# Revit family: Pump_Commercial-Sewage_Dewatering-Zoeller-64HD_Single_Seal_6-Series
name_source: partatom
category: Mechanical Equipment
revit_build: Autodesk Revit 2014 (Build: 20130308_1515(x64)
units: mm (PartAtom-declared; Revit-internal decimal feet)

## types (7) — shared parameters
Assembly Code = D2090
Connection Description = 6" Horizontal Discharge
Default Elevation = 0"
Description = Heavy Duty Solids-Handling Pumps
Discharge Diameter = 6"
Discharge Radius = 3"
Flange = ANSI B16.1
Height = 47 1/8"
Hertz = 60
High Temperature (5-10 BHP) = No
Impeller Type = 2 Vane Enclosed
Installation Type = Floor Mounted
Insulation = Class F
Inverted Duty = No
Length = 27 1/8"
Manufacturer = Zoeller
Material = Cast Iron-Zoeller-Powder Coated Epoxy
Max. Stator Temp. = 311 °F
Max. Water Temp. = 104 °F
Min. Recommended Fluid Level = 24"
Moisture Sensor (Optional) = Moisture Sensing Probes (Requires a circuit in control panel)
Motor Design Letter = NEMA B
Motor Shaft = 416 SS
Motor Thermal Shutoff (Single Phase Only) = Thermal Sensors With Automatic Reset
Motor Type = Standard Submersible
O-Rings (Optional) Viton = No
O-Rings and Cover Gasket = Buna-N
Operation = Non-Automatic
Phase = 3
Power Cord = 25' (7.6 m) #2-4 SO
Price = Prices may vary. Please consult Manufacturer Representative for most up-to-date price list.
Product Documentation Link = http://cdn.qleapahead.com
Product Page URL = http://www.zoellerengprod.com
Pump Net Weight: lbs. (kg) = 850 lbs. (386 kg)
RPM = 1725
Rail System Discharge = 6"
Sensor Cord Size = #16-5 SO
Shaft Seal (Standard) = Carbon/Ceramic
Shaft Seal Lower (Options) = Carbon/Silicon Carbide, Silicon Carbide/Silicon Carbide
Shaft Seal Upper (Options) = Silicon Carbide/Carbon, Silicon Carbide/Silicon Carbide
Solid Size = 4" (100 mm)
Tandem Seals = Standard
Trimmed Impeller = No
URL = http://www.zoellerpumps.com
Warranty Information = 36 Months (Limited)
Waste Connection = Yes
Width = 22 1/8"

## per-type parameters (varying)
| type | Amps | Apparent Load | Impeller Diameter | Locked Rotor Amps (Voltage Dependant) | Max. Flow @ 20' | Max. Flow @ 35' | Max. Flow @ 40' | Max. Head | Maximum KW Input | Model | Motor | NEC Locked Rotor Code | Service Factor | Voltage |
| F6424 - 230V/3Ph/68A/25BHP | 68 A | 15640 VA | 9 1/8" | 314 | 1900 GPM | 0 GPM | 0 GPM | 70' | 24.2 | F6424 | 25 | F | 1.2 | 230 V |
| G6424 - 460V/3Ph/34A/25BHP | 34 A | 15640 VA | 9 1/8" | 157 | 1900 GPM | 0 GPM | 0 GPM | 70' | 24.2 | G6424 | 25 | F | 1.2 | 460 V |
| F6425 - 230V/3Ph/80A/30BHP | 80 A | 18400 VA | 9 1/2" | 360 | 2100 GPM | 0 GPM | 0 GPM | 83' | 28.1 | F6425 | 30 | E | 1.2 | 230 V |
| G6425 - 460V/3Ph/40A/30BHP | 40 A | 18400 VA | 9 1/2" | 180 | 2100 GPM | 0 GPM | 0 GPM | 83' | 28.1 | G6425 | 30 | E | 1.2 | 460 V |
| G6426 - 460V/3Ph/52A/40BHP | 52 A | 23920 VA | 10 1/8" | 240 | 2460 GPM | 0 GPM | 0 GPM | 101' | 36.0 | G6426 | 40 | E | 1.2 | 460 V |
| G6427 - 460V/3Ph/62A/50BHP | 62 A | 28520 VA | 10 5/8" | 278 | 0 GPM | 2425 GPM | 0 GPM | 115' | 42.5 | G6427 | 50 | D | 1.2 | 460 V |
| G6428 - 460V/3Ph/75A/60BHP | 75 A | 34500 VA | 11" | 278 | 0 GPM | 0 GPM | 2600 GPM | 125' | 50 | G6428 | 60 | C | 1 | 460 V |

## geometry (parser evidence)
native form markers: Sweep x1
no freeform markers — native parametric forms only
